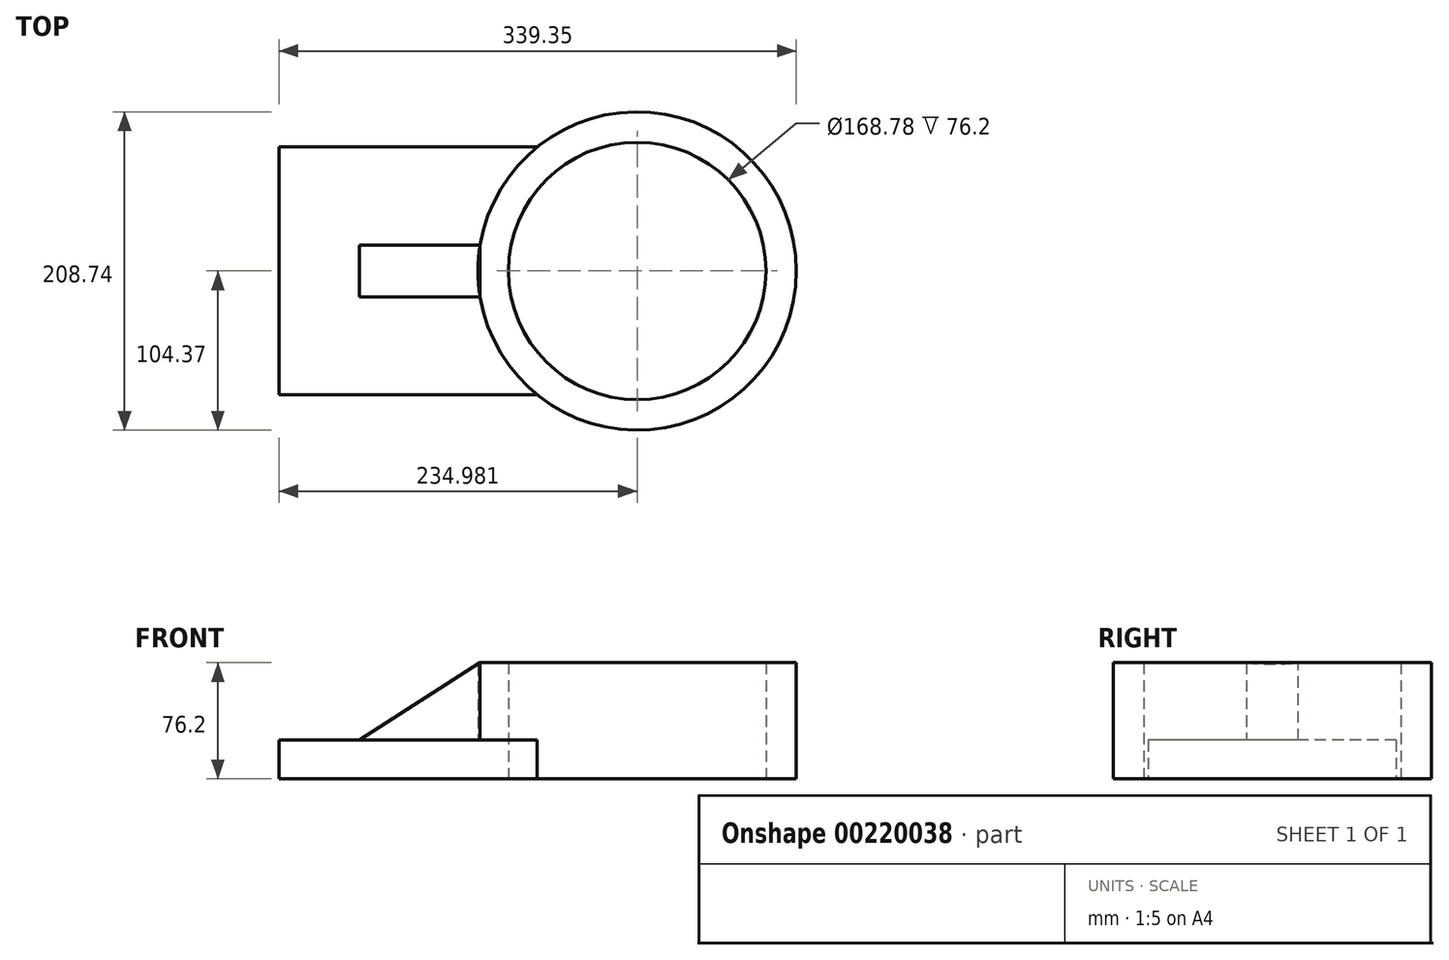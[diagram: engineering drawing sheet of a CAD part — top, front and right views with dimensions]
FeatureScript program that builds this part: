
annotation { "Feature Type Name" : "Feature", "Feature Type Description" : "" }
export const myFeature = defineFeature(function(context is Context, id is Id, definition is map)
    precondition{}
    {
        {
            var Q0;
            Q0=qCreatedBy(makeId("Top.planeOp"),FACE);
            var sketch = newSketch(context, id + "F0", { "sketchPlane" : qUnion([Q0])});
            skLineSegment(sketch, "E0.bottom", {"start": v(76.44, 75.78) * mm, "end": v(-76.44, 75.78) * mm});
            skLineSegment(sketch, "E0.top", {"start": v(76.44, -75.78) * mm, "end": v(-76.44, -75.78) * mm});
            skLineSegment(sketch, "E0.right", {"start": v(-76.44, 75.78) * mm, "end": v(-76.44, -75.78) * mm});
            skPoint(sketch, "E0.middle", {"position": v(0, 0) * mm});
            skCircle(sketch, "E1", {"center": v(148.21, 0) * mm, "radius": 104.37 * mm});
            skPoint(sketch, "E1.third.point", {"position": v(252.3, 7.73) * mm});
            skCircle(sketch, "E2", {"center": v(148.21, 0) * mm, "radius": 84.4 * mm});
            skLineSegment(sketch, "E3.bottom", {"start": v(44.55, 12.15) * mm, "end": v(-33.06, 12.15) * mm});
            skLineSegment(sketch, "E3.right", {"start": v(-33.06, 12.15) * mm, "end": v(-33.06, -12.15) * mm});
            skPoint(sketch, "E3.middle", {"position": v(43.84, 0) * mm});
            skPoint(sketch, "E3.left.start.orphan", {"position": v(120.74, 12.15) * mm});
            skPoint(sketch, "E4.orphan", {"position": v(120.74, -12.15) * mm});
            skLineSegment(sketch, "E5", {"start": v(-33.06, -12.15) * mm, "end": v(44.55, -12.15) * mm});
            skSolve(sketch);
        }
        {
            var Q0;
            Q0=makeQuery(id+"F0.imprint","IMPRINT",FACE,{"disambiguationData":[TD([[makeQuery(id+"F0.imprint","IMPRINT",EDGE,{"derivedFrom":sQuery(id+"F0.wireOp",EDGE,"E2")}),-1.0]])]});
            extrude(context, id + "F1", {"entities" : qUnion([Q0]), "depth" : 76.2 * mm});
        }
        {
            var Q0;
            Q0=qCreatedBy(makeId("Top.planeOp"),FACE);
            var sketch = newSketch(context, id + "F2", { "sketchPlane" : qUnion([Q0])});
            skLineSegment(sketch, "E6.bottom", {"start": v(82.7, 81.25) * mm, "end": v(-86.77, 81.25) * mm});
            skLineSegment(sketch, "E6.top", {"start": v(82.7, -81.25) * mm, "end": v(-86.77, -81.25) * mm});
            skLineSegment(sketch, "E6.right", {"start": v(-86.77, 81.25) * mm, "end": v(-86.77, -81.25) * mm});
            skPoint(sketch, "E6.middle", {"position": v(0, 0) * mm});
            skCircle(sketch, "E7.0", {"center": v(148.21, 0) * mm, "radius": 104.37 * mm});
            skPoint(sketch, "E8.orphan", {"position": v(86.77, 81.25) * mm});
            skPoint(sketch, "E9.orphan", {"position": v(86.77, -81.25) * mm});
            skSolve(sketch);
        }
        {
            var Q0;
            {var subQ0=sQuery(id+"F2.wireOp",EDGE,"E6.bottom");Q0=makeQuery(id+"F2.imprint","IMPRINT",FACE,{"disambiguationData":[TD([[makeQuery(id+"F2.imprint","IMPRINT",EDGE,{"derivedFrom":subQ0}),1.0]])]});}
            extrude(context, id + "F3", {"entities" : qUnion([Q0]), "operationType" : NewBodyOperationType.ADD, "depth" : 25.4 * mm});
        }
        {
            var Q0;
            Q0=makeQuery(id+"F3.opExtrude","CAP_FACE",FACE,{"disambiguationData":[OSD([sQuery(id+"F2.wireOp",EDGE,"E6.bottom"),sQuery(id+"F2.wireOp",EDGE,"E6.top"),sQuery(id+"F2.wireOp",EDGE,"E6.right"),sQuery(id+"F2.wireOp",EDGE,"E7.0")])],"isStart":false});
            var sketch = newSketch(context, id + "F4", { "sketchPlane" : qUnion([Q0])});
            skLineSegment(sketch, "E10.bottom", {"start": v(45.23, 17) * mm, "end": v(-33.9, 17) * mm});
            skLineSegment(sketch, "E10.top", {"start": v(45.23, -17) * mm, "end": v(-33.9, -17) * mm});
            skLineSegment(sketch, "E10.right", {"start": v(-33.9, 17) * mm, "end": v(-33.9, -17) * mm});
            skPoint(sketch, "E10.middle", {"position": v(43.84, 0) * mm});
            skCircle(sketch, "E11.0", {"center": v(148.21, 0) * mm, "radius": 104.37 * mm});
            skPoint(sketch, "E10.left.start.orphan", {"position": v(121.58, 17) * mm});
            skPoint(sketch, "E12.orphan", {"position": v(121.58, -17) * mm});
            skSolve(sketch);
        }
        {
            var Q0;
            {var subQ0=sQuery(id+"F4.wireOp",EDGE,"E10.bottom");Q0=makeQuery(id+"F4.imprint","IMPRINT",FACE,{"disambiguationData":[TD([[makeQuery(id+"F4.imprint","IMPRINT",EDGE,{"derivedFrom":subQ0}),1.0]])]});}
            var Q1;
            Q1=makeQuery(id+"F1.opExtrude","CAP_FACE",FACE,{"disambiguationData":[OSD([sQuery(id+"F0.wireOp",EDGE,"E1"),sQuery(id+"F0.wireOp",EDGE,"E2")])],"isStart":false});
            extrude(context, id + "F5", {"entities" : qUnion([Q0]), "endBound" : BoundingType.UP_TO_SURFACE, "endBoundEntityFace" : qUnion([Q1]), "depth" : 46.23 * mm});
        }
        {
            var Q0;
            Q0=makeQuery(id+"F5.opExtrude","SWEPT_FACE",FACE,{"disambiguationData":[OSD([sQuery(id+"F4.wireOp",EDGE,"E10.top")])]});
            var sketch = newSketch(context, id + "F6", { "sketchPlane" : qUnion([Q0])});
            skLineSegment(sketch, "E13.0", {"start": v(45.23, 76.2) * mm, "end": v(45.23, 25.4) * mm});
            skLineSegment(sketch, "E14.0", {"start": v(82.7, 25.4) * mm, "end": v(-86.77, 25.4) * mm});
            skLineSegment(sketch, "E15", {"start": v(-33.9, 25.4) * mm, "end": v(45.23, 76.2) * mm});
            skLineSegment(sketch, "E16", {"start": v(-33.9, 25.4) * mm, "end": v(-33.9, 76.2) * mm});
            skLineSegment(sketch, "E17", {"start": v(-33.9, 76.2) * mm, "end": v(45.23, 76.2) * mm});
            skSolve(sketch);
        }
        {
            var Q0;
            Q0=makeQuery(id+"F6.imprint","IMPRINT",FACE,{"disambiguationData":[TD([[makeQuery(id+"F6.imprint","IMPRINT",EDGE,{"derivedFrom":sQuery(id+"F6.wireOp",EDGE,"E15")}),1.0]])]});
            extrude(context, id + "F7", {"entities" : qUnion([Q0]), "operationType" : NewBodyOperationType.REMOVE, "endBound" : BoundingType.THROUGH_ALL, "oppositeDirection" : true, "depth" : 25.4 * mm});
        }
    });
